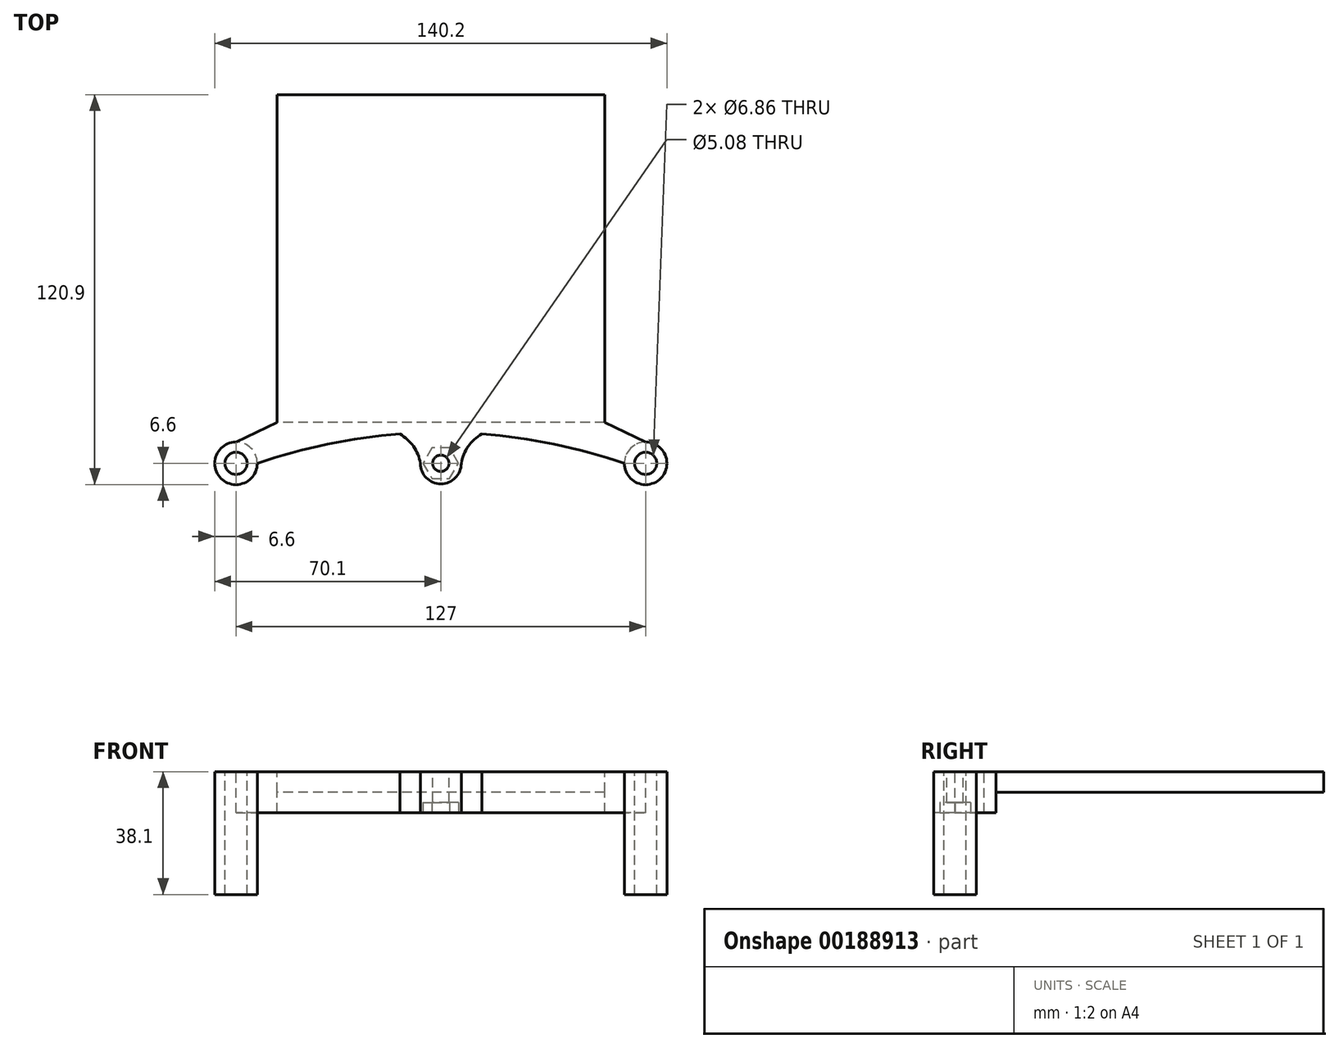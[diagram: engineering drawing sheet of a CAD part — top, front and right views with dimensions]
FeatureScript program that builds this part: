
annotation { "Feature Type Name" : "Feature", "Feature Type Description" : "" }
export const myFeature = defineFeature(function(context is Context, id is Id, definition is map)
    precondition{}
    {
        {
            var Q0;
            Q0=qCreatedBy(makeId("Top.planeOp"),FACE);
            var sketch = newSketch(context, id + "F0", { "sketchPlane" : qUnion([Q0])});
            skLineSegment(sketch, "E0.bottom", {"start": v(50.8, 50.8) * mm, "end": v(-50.8, 50.8) * mm});
            skLineSegment(sketch, "E0.top", {"start": v(50.8, -50.8) * mm, "end": v(-50.8, -50.8) * mm});
            skLineSegment(sketch, "E0.left", {"start": v(50.8, 50.8) * mm, "end": v(50.8, -50.8) * mm});
            skLineSegment(sketch, "E0.right", {"start": v(-50.8, 50.8) * mm, "end": v(-50.8, -50.8) * mm});
            skPoint(sketch, "E0.middle", {"position": v(0, 0) * mm});
            skSolve(sketch);
        }
        {
            var Q0;
            Q0=qSketchRegion(id+"F0",true);
            extrude(context, id + "F1", {"entities" : qUnion([Q0]), "oppositeDirection" : true, "depth" : 6.35 * mm});
        }
        {
            var Q0;
            Q0=makeQuery(id+"F1.opExtrude","CAP_FACE",FACE,{"disambiguationData":[OSD([sQuery(id+"F0.wireOp",EDGE,"E0.bottom"),sQuery(id+"F0.wireOp",EDGE,"E0.top"),sQuery(id+"F0.wireOp",EDGE,"E0.left"),sQuery(id+"F0.wireOp",EDGE,"E0.right")])],"isStart":true});
            var sketch = newSketch(context, id + "F2", { "sketchPlane" : qUnion([Q0])});
            skCircle(sketch, "E1", {"center": v(-63.5, -63.5) * mm, "radius": 3.43 * mm});
            skCircle(sketch, "E2", {"center": v(63.5, -63.5) * mm, "radius": 3.43 * mm});
            skLineSegment(sketch, "E3", {"start": v(-63.5, -63.5) * mm, "end": v(0, -50.8) * mm, "construction": true});
            skLineSegment(sketch, "E4", {"start": v(0, -50.8) * mm, "end": v(63.5, -63.5) * mm, "construction": true});
            skLineSegment(sketch, "E5", {"start": v(-63.5, -63.5) * mm, "end": v(63.5, -63.5) * mm, "construction": true});
            skArc(sketch, "E6", {"start": v(-63.5, -56.9) * mm, "mid": v(-68.17, -68.17) * mm, "end": v(-56.9, -63.5) * mm});
            skArc(sketch, "E7", {"start": v(56.9, -63.5) * mm, "mid": v(68.17, -68.17) * mm, "end": v(63.5, -56.9) * mm});
            skLineSegment(sketch, "E8", {"start": v(-63.5, -56.9) * mm, "end": v(-50.8, -50.8) * mm});
            skLineSegment(sketch, "E9", {"start": v(-63.5, -63.5) * mm, "end": v(-63.5, -56.9) * mm, "construction": true});
            skArc(sketch, "E10", {"start": v(56.9, -63.5) * mm, "mid": v(35.1, -57.54) * mm, "end": v(12.7, -54.44) * mm});
            skLineSegment(sketch, "E11", {"start": v(50.8, -50.8) * mm, "end": v(63.5, -56.9) * mm});
            skLineSegment(sketch, "E12", {"start": v(63.5, -56.9) * mm, "end": v(63.5, -63.5) * mm, "construction": true});
            skCircle(sketch, "E13", {"center": v(0, -63.5) * mm, "radius": 6.35 * mm});
            skArc(sketch, "E14", {"start": v(-6.35, -63.5) * mm, "mid": v(-8.49, -58.24) * mm, "end": v(-12.7, -54.44) * mm});
            skArc(sketch, "E15", {"start": v(12.7, -54.44) * mm, "mid": v(8.49, -58.24) * mm, "end": v(6.35, -63.5) * mm});
            skCircle(sketch, "E16", {"center": v(0, -63.5) * mm, "radius": 2.54 * mm});
            skLineSegment(sketch, "E17", {"start": v(-12.7, -54.44) * mm, "end": v(0, -63.5) * mm, "construction": true});
            skLineSegment(sketch, "E18", {"start": v(12.7, -54.44) * mm, "end": v(0, -63.5) * mm, "construction": true});
            skLineSegment(sketch, "E19", {"start": v(-12.7, -54.44) * mm, "end": v(12.7, -54.44) * mm, "construction": true});
            skArc(sketch, "E20.trimOffspring", {"start": v(-12.7, -54.44) * mm, "mid": v(-35.1, -57.54) * mm, "end": v(-56.9, -63.5) * mm});
            skSolve(sketch);
        }
        {
            var Q0;
            Q0=makeQuery(id+"F2.imprint","IMPRINT",FACE,{"disambiguationData":[TD([[makeQuery(id+"F2.imprint","IMPRINT",EDGE,{"derivedFrom":sQuery(id+"F2.wireOp",EDGE,"E1")}),-1.0]])]});
            var Q1;
            Q1=makeQuery(id+"F2.imprint","IMPRINT",FACE,{"disambiguationData":[TD([[makeQuery(id+"F2.imprint","IMPRINT",EDGE,{"derivedFrom":sQuery(id+"F2.wireOp",EDGE,"E16")}),-1.0]])]});
            extrude(context, id + "F3", {"entities" : qUnion([Q0, Q1]), "operationType" : NewBodyOperationType.ADD, "oppositeDirection" : true, "depth" : 12.7 * mm});
        }
        {
            var Q0;
            Q0=makeQuery(id+"F3.opExtrude","CAP_FACE",FACE,{"disambiguationData":[OSD([sQuery(id+"F0.wireOp",EDGE,"E0.top"),sQuery(id+"F2.wireOp",EDGE,"E1"),sQuery(id+"F2.wireOp",EDGE,"E2"),sQuery(id+"F2.wireOp",EDGE,"E6"),sQuery(id+"F2.wireOp",EDGE,"E7"),sQuery(id+"F2.wireOp",EDGE,"E8"),sQuery(id+"F2.wireOp",EDGE,"E10"),sQuery(id+"F2.wireOp",EDGE,"E11"),sQuery(id+"F2.wireOp",EDGE,"E13"),sQuery(id+"F2.wireOp",EDGE,"E14"),sQuery(id+"F2.wireOp",EDGE,"E15"),sQuery(id+"F2.wireOp",EDGE,"E16"),sQuery(id+"F2.wireOp",EDGE,"E20.trimOffspring")])],"isStart":false});
            var sketch = newSketch(context, id + "F4", { "sketchPlane" : qUnion([Q0])});
            skCircle(sketch, "E21.0", {"center": v(-63.5, 63.5) * mm, "radius": 3.43 * mm});
            skArc(sketch, "E21.1", {"start": v(-63.5, 56.9) * mm, "mid": v(-68.17, 68.17) * mm, "end": v(-56.9, 63.5) * mm});
            skArc(sketch, "E22", {"start": v(-63.5, 56.9) * mm, "mid": v(-58.83, 58.83) * mm, "end": v(-56.9, 63.5) * mm});
            skArc(sketch, "E23.MirrorCS", {"start": v(63.5, 56.9) * mm, "mid": v(58.83, 58.83) * mm, "end": v(56.9, 63.5) * mm});
            skCircle(sketch, "E24.MirrorC", {"center": v(63.5, 63.5) * mm, "radius": 3.43 * mm});
            skArc(sketch, "E25.MirrorCS", {"start": v(63.5, 56.9) * mm, "mid": v(68.17, 68.17) * mm, "end": v(56.9, 63.5) * mm});
            skSolve(sketch);
        }
        {
            var Q0;
            Q0=qSketchRegion(id+"F4",true);
            extrude(context, id + "F5", {"entities" : qUnion([Q0]), "operationType" : NewBodyOperationType.ADD, "depth" : 25.4 * mm});
        }
        {
            var Q0;
            Q0=makeQuery(id+"F3.opExtrude","CAP_FACE",FACE,{"disambiguationData":[OSD([sQuery(id+"F0.wireOp",EDGE,"E0.top"),sQuery(id+"F2.wireOp",EDGE,"E1"),sQuery(id+"F2.wireOp",EDGE,"E2"),sQuery(id+"F2.wireOp",EDGE,"E6"),sQuery(id+"F2.wireOp",EDGE,"E7"),sQuery(id+"F2.wireOp",EDGE,"E8"),sQuery(id+"F2.wireOp",EDGE,"E10"),sQuery(id+"F2.wireOp",EDGE,"E11"),sQuery(id+"F2.wireOp",EDGE,"E13"),sQuery(id+"F2.wireOp",EDGE,"E14"),sQuery(id+"F2.wireOp",EDGE,"E15"),sQuery(id+"F2.wireOp",EDGE,"E16"),sQuery(id+"F2.wireOp",EDGE,"E20.trimOffspring")])],"isStart":false});
            var sketch = newSketch(context, id + "F6", { "sketchPlane" : qUnion([Q0])});
            skCircle(sketch, "E26.cCircle", {"center": v(0, 63.5) * mm, "radius": 4.76 * mm, "construction": true});
            skLineSegment(sketch, "E26.0", {"start": v(-2.75, 68.26) * mm, "end": v(2.75, 68.26) * mm});
            skLineSegment(sketch, "E26.1", {"start": v(2.75, 68.26) * mm, "end": v(5.5, 63.5) * mm});
            skLineSegment(sketch, "E26.2", {"start": v(5.5, 63.5) * mm, "end": v(2.75, 58.74) * mm});
            skLineSegment(sketch, "E26.3", {"start": v(2.75, 58.74) * mm, "end": v(-2.75, 58.74) * mm});
            skLineSegment(sketch, "E26.4", {"start": v(-2.75, 58.74) * mm, "end": v(-5.5, 63.5) * mm});
            skLineSegment(sketch, "E26.5", {"start": v(-5.5, 63.5) * mm, "end": v(-2.75, 68.26) * mm});
            skPoint(sketch, "E26.0.midPoint", {"position": v(0, 68.26) * mm});
            skSolve(sketch);
        }
        {
            var Q0;
            Q0=makeQuery(id+"F6.imprint","IMPRINT",FACE,{"disambiguationData":[TD([[makeQuery(id+"F6.imprint","IMPRINT",EDGE,{"derivedFrom":sQuery(id+"F6.wireOp",EDGE,"E26.0")}),-1.0]])]});
            extrude(context, id + "F7", {"entities" : qUnion([Q0]), "operationType" : NewBodyOperationType.REMOVE, "oppositeDirection" : true, "depth" : 3.17 * mm});
        }
    });
